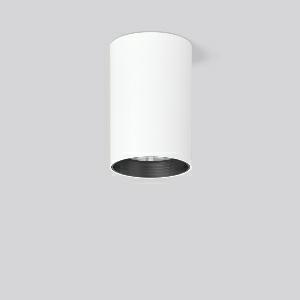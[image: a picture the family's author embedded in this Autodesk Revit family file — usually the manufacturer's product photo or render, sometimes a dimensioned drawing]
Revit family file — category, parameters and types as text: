
# Revit family: heledon_maxi_a_931227_002_57e4
name_source: partatom
category: Lighting Fixtures
units: mm (PartAtom-declared; Revit-internal decimal feet)

## family parameters
Cut with Voids When Loaded = No
Host = Face
Light Source = No
Part Type = Normal
Room Calculation Point = No
Round Connector Dimension = Use Diameter
Shared = No

## types (1)
- HELEDON maxi A (1 x LED Modul 930, 3650 lm, 3000)
    Apparent Load = 35 VA
    Approval mark = CE
    CIE Flux Codes = 97 100 100 100 100
    Color Rendering = 90
    Color Temperature = 3000
    Default Elevation = 1800 mm
    Description = Series: HELEDON maxi
Cylindrical surface-mounted downlight. Housing: die-cast aluminium, powder-coated. Internal ceiling frame polycarbonate with bayonet mounting. Black plastic ring and recessed LED to prevent glare from the side. Optical assembly with lens made of plastic (polycarbonate) for the best homogeneous light distribution - can be changed without tools. Best colour rendering index Ra>90. Suitable for Ceiling mounting. Easy installation with a separate ceiling frame with bayonet mounting and plug connection. Driver integrated. Connected via plug-in connector. High quality converter without flickering and stroboscopic effect. The following accessories can be mounted without use of tools: interchangeable lenses, decorative glasses, honeycomb louvre, clear and frosted diffusers, white interchangeable plastic ring. 
Colour: traffic white, matt (RAL 9016)
Diameter: 123 mm
Height: 183 mm
Lamp: LED
Socket: without socket
Colour temperature: 3000K
Colour rendering index (CRI): 92
System power: 35 W
Rated luminous flux: 3650 lm
Luminous efficiency: 104 lm/W
Control gear: Regulated power supply
Protection class: I
Type of protection: IP 20
    Height = 183 mm
    Lamp = 1 x LED Modul 930
    Lamp Light Flux = 3650 lm
    Lamp count = 1
    Length = 123 mm
    Lifetime = 50000 h
    Luminous efficacy = 104 lm/W
    Manufacturer = RZB
    ModVariant = No
    Model = 931227.002
    Mounting Place = Ceiling
    Mounting Type = Surface mounted
    Number of Poles = 1
    OnlyDefault = Yes
    Power Factor = 1
    Product Name = HELEDON maxi A
    Product group = Surface mounted downlights
    ProductGroupID = 302
    Protection Class = Protection class I
    Protection Degree = IP 20
    RLX_Detail_Level = 1
    RLX_Emergency_Light_Flux = 0 lm
    RLX_Emergency_Type = 0
    RLX_Emergency_Type_DB = No
    RlxData = <blob elided: 97945 chars, md5=e5833d54>
    Socket = socket
    Standby Power = 0 W
    System Light Flux = 3650 lm
    System Power = 35 W
    Type Comments = Product without accessories
    Type Image = 931193.002.jpg
    URL = http://relux.com
    VarID = ---
    Voltage = 230 V
    Voltage Range = 220-240 V
    Weight = 0.00 kg
    Width = 0 mm  [stored 0 ft]

note: [stored X ft] marks values corroborated as IEEE doubles in the binary element streams (Revit-internal decimal feet)

## geometry (parser evidence)
native form markers: Blend x4, Sweep x10
no freeform markers — native parametric forms only
